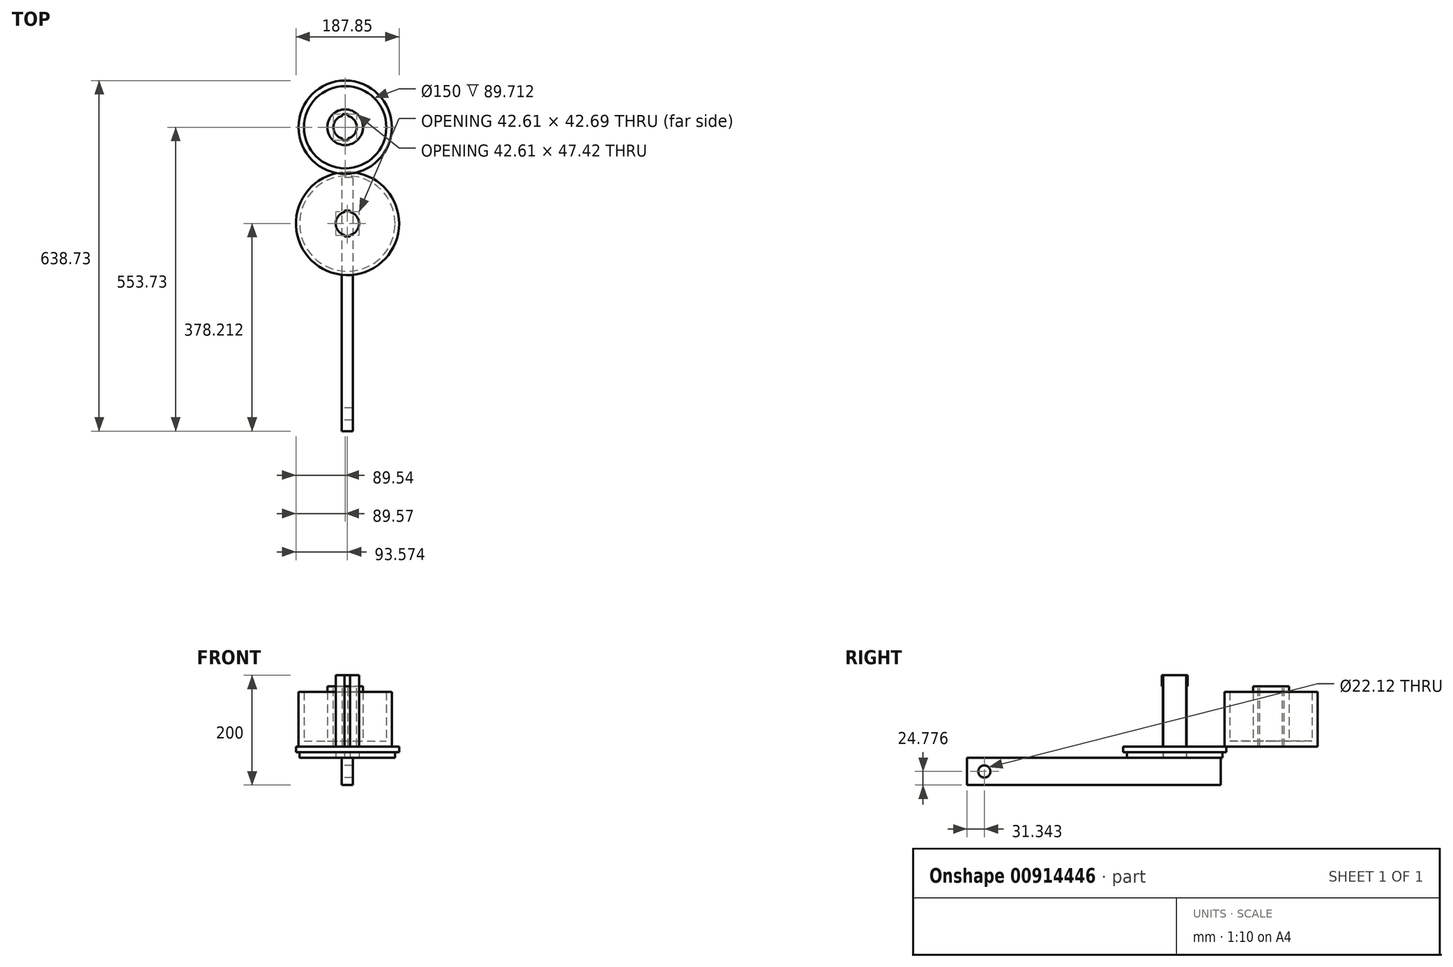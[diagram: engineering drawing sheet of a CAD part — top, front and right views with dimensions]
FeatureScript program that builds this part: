
annotation { "Feature Type Name" : "Feature", "Feature Type Description" : "" }
export const myFeature = defineFeature(function(context is Context, id is Id, definition is map)
    precondition{}
    {
        {
            var Q0;
            Q0=qCreatedBy(makeId("Front.planeOp"),FACE);
            var sketch = newSketch(context, id + "F0", { "sketchPlane" : qUnion([Q0])});
            skLineSegment(sketch, "E0", {"start": v(-85, 100) * mm, "end": v(-85, 0) * mm});
            skLineSegment(sketch, "E1", {"start": v(-85, 0) * mm, "end": v(0, 0) * mm});
            skLineSegment(sketch, "E2", {"start": v(0, 0) * mm, "end": v(0, 10) * mm});
            skLineSegment(sketch, "E3", {"start": v(0, 10) * mm, "end": v(-75, 10) * mm});
            skLineSegment(sketch, "E4", {"start": v(-75, 10) * mm, "end": v(-75, 99.71) * mm});
            skLineSegment(sketch, "E5", {"start": v(-75, 99.71) * mm, "end": v(-85, 100) * mm});
            skSolve(sketch);
        }
        {
            var Q0;
            Q0=makeQuery(id+"F0.imprint","IMPRINT",FACE,{"disambiguationData":[TD([[makeQuery(id+"F0.imprint","IMPRINT",EDGE,{"derivedFrom":sQuery(id+"F0.wireOp",EDGE,"E0")}),1.0]])]});
            var Q1;
            Q1=sQuery(id+"F0.wireOp",EDGE,"E2");
            revolve(context, id + "F1", {"surfaceOperationType" : NewSurfaceOperationType.NEW, "entities" : qUnion([Q0]), "axis" : qUnion([Q1]), "revolveType" : RevolveType.ONE_DIRECTION, "angle" : 360 * degree});
        }
        {
            var Q0;
            Q0=qCreatedBy(makeId("Top.planeOp"),FACE);
            cPlane(context, id + "F2", {"entities" : qUnion([Q0]), "cplaneType" : CPlaneType.OFFSET, "offset" : 110 * mm, "width" : 150 * mm, "height" : 150 * mm});
        }
        {
            var Q0;
            Q0=qCreatedBy(makeId("Top.planeOp"),FACE);
            var sketch = newSketch(context, id + "F3", { "sketchPlane" : qUnion([Q0])});
            skCircle(sketch, "E6", {"center": v(0, 0) * mm, "radius": 32.5 * mm});
            skSolve(sketch);
        }
        {
            var Q0;
            Q0 = qSketchRegion(id + "F3", true);
            extrude(context, id + "F4", {"entities" : qUnion([Q0]), "operationType" : NewBodyOperationType.ADD, "depth" : 110 * mm, "offsetDistance" : 25 * mm});
        }
        {
            var Q0;
            Q0=qCreatedBy(id+"F2.planeOp",FACE);
            cPlane(context, id + "F5", {"entities" : qUnion([Q0]), "cplaneType" : CPlaneType.OFFSET, "offset" : 30 * mm, "width" : 150 * mm, "height" : 150 * mm});
        }
        {
            var Q0;
            Q0=qCreatedBy(id+"F5.planeOp",FACE);
            var sketch = newSketch(context, id + "F6", { "sketchPlane" : qUnion([Q0])});
            skLineSegment(sketch, "E7", {"start": v(4.87, 23.7) * mm, "end": v(-5.13, 23.7) * mm});
            skLineSegment(sketch, "E8", {"start": v(-5.13, 23.7) * mm, "end": v(-5.13, 20.7) * mm});
            skLineSegment(sketch, "E9", {"start": v(4.87, 23.7) * mm, "end": v(4.87, 20.7) * mm});
            skArc(sketch, "E10", {"start": v(-5.13, 20.7) * mm, "mid": v(-21.33, 0) * mm, "end": v(-5.13, -20.7) * mm});
            skArc(sketch, "E11", {"start": v(4.87, 20.7) * mm, "mid": v(21.27, 0) * mm, "end": v(4.87, -20.7) * mm});
            skLineSegment(sketch, "E12", {"start": v(-5.13, -20.7) * mm, "end": v(-5.13, -23.7) * mm});
            skLineSegment(sketch, "E13", {"start": v(-5.13, -23.7) * mm, "end": v(4.87, -23.7) * mm});
            skLineSegment(sketch, "E14", {"start": v(4.87, -23.7) * mm, "end": v(4.87, -20.7) * mm});
            skSolve(sketch);
        }
        {
            var Q0;
            Q0=makeQuery(id+"F6.imprint","IMPRINT",FACE,{"disambiguationData":[TD([[makeQuery(id+"F6.imprint","IMPRINT",EDGE,{"derivedFrom":sQuery(id+"F6.wireOp",EDGE,"E7")}),1.0]])]});
            extrude(context, id + "F7", {"entities" : qUnion([Q0]), "operationType" : NewBodyOperationType.REMOVE, "oppositeDirection" : true, "depth" : 150 * mm, "offsetDistance" : 25 * mm});
        }
        {
            var Q0;
            Q0=qCreatedBy(id+"F2.planeOp",FACE);
            var sketch = newSketch(context, id + "F8", { "sketchPlane" : qUnion([Q0])});
            skLineSegment(sketch, "E15", {"start": v(8.9, -151.8) * mm, "end": v(-1.1, -151.8) * mm});
            skLineSegment(sketch, "E16", {"start": v(-1.1, -151.8) * mm, "end": v(-1.1, -154.8) * mm});
            skLineSegment(sketch, "E17", {"start": v(8.9, -151.8) * mm, "end": v(8.9, -154.8) * mm});
            skArc(sketch, "E18", {"start": v(-1.1, -154.8) * mm, "mid": v(-17.3, -175.52) * mm, "end": v(-1.1, -196.23) * mm});
            skArc(sketch, "E19", {"start": v(8.9, -154.8) * mm, "mid": v(25.3, -175.52) * mm, "end": v(8.9, -196.23) * mm});
            skLineSegment(sketch, "E20", {"start": v(-1.1, -196.23) * mm, "end": v(-1.1, -199.23) * mm});
            skLineSegment(sketch, "E21", {"start": v(-1.1, -199.23) * mm, "end": v(8.9, -199.23) * mm});
            skLineSegment(sketch, "E22", {"start": v(8.9, -199.23) * mm, "end": v(8.9, -196.23) * mm});
            skSolve(sketch);
        }
        {
            var Q0;
            Q0=makeQuery(id+"F8.imprint","IMPRINT",FACE,{"disambiguationData":[TD([[makeQuery(id+"F8.imprint","IMPRINT",EDGE,{"derivedFrom":sQuery(id+"F8.wireOp",EDGE,"E15")}),1.0]])]});
            extrude(context, id + "F9", {"entities" : qUnion([Q0]), "depth" : 20 * mm, "offsetDistance" : 25 * mm});
        }
        {
            var Q0;
            Q0=makeQuery(id+"F9.opExtrude","CAP_FACE",FACE,{"disambiguationData":[OSD([sQuery(id+"F8.wireOp",EDGE,"E15"),sQuery(id+"F8.wireOp",EDGE,"E16"),sQuery(id+"F8.wireOp",EDGE,"E17"),sQuery(id+"F8.wireOp",EDGE,"E18"),sQuery(id+"F8.wireOp",EDGE,"E19"),sQuery(id+"F8.wireOp",EDGE,"E20"),sQuery(id+"F8.wireOp",EDGE,"E21"),sQuery(id+"F8.wireOp",EDGE,"E22")])],"isStart":true});
            var sketch = newSketch(context, id + "F10", { "sketchPlane" : qUnion([Q0])});
            skCircle(sketch, "E23", {"center": v(4.03, 175.52) * mm, "radius": 21.35 * mm});
            skSolve(sketch);
        }
        {
            var Q0;
            {var subQ7=makeQuery(id+"F9.opExtrude","CAP_EDGE",EDGE,{"disambiguationData":[OSD([sQuery(id+"F8.wireOp",EDGE,"E18")])],"isStart":true});Q0=makeQuery(id+"F10.imprint","IMPRINT",FACE,{"disambiguationData":[TD([[makeQuery(id+"F10.imprint","IMPRINT",EDGE,{"derivedFrom":subQ7}),-1.0]])]});}
            extrude(context, id + "F11", {"entities" : qUnion([Q0]), "operationType" : NewBodyOperationType.ADD, "depth" : 130 * mm, "offsetDistance" : 25 * mm});
        }
        {
            var Q0;
            Q0=qCreatedBy(makeId("Top.planeOp"),FACE);
            cPlane(context, id + "F12", {"entities" : qUnion([Q0]), "cplaneType" : CPlaneType.OFFSET, "offset" : 20 * mm, "oppositeDirection" : true, "width" : 150 * mm, "height" : 150 * mm});
        }
        {
            var Q0;
            Q0=makeQuery(id+"F11.opExtrude","CAP_FACE",FACE,{"disambiguationData":[OSD([sQuery(id+"F8.wireOp",EDGE,"E16"),sQuery(id+"F8.wireOp",EDGE,"E17"),sQuery(id+"F8.wireOp",EDGE,"E18"),sQuery(id+"F8.wireOp",EDGE,"E19"),sQuery(id+"F8.wireOp",EDGE,"E20"),sQuery(id+"F8.wireOp",EDGE,"E22"),sQuery(id+"F10.wireOp",EDGE,"E23")])],"isStart":false});
            var sketch = newSketch(context, id + "F13", { "sketchPlane" : qUnion([Q0])});
            skCircle(sketch, "E24", {"center": v(4.03, 175.52) * mm, "radius": 86.95 * mm});
            skSolve(sketch);
        }
        {
            var Q0;
            Q0=makeQuery(id+"F13.imprint","IMPRINT",FACE,{"disambiguationData":[TD([[makeQuery(id+"F13.imprint","IMPRINT",EDGE,{"derivedFrom":sQuery(id+"F13.wireOp",EDGE,"E24")}),1.0]])]});
            extrude(context, id + "F14", {"entities" : qUnion([Q0]), "oppositeDirection" : true, "depth" : 10 * mm, "offsetDistance" : 25 * mm});
        }
        {
            var Q0;
            Q0=qCreatedBy(id+"F12.planeOp",FACE);
            cPlane(context, id + "F15", {"entities" : qUnion([Q0]), "cplaneType" : CPlaneType.OFFSET, "offset" : 20 * mm, "width" : 150 * mm, "height" : 150 * mm});
        }
        {
            var Q0;
            Q0=qCreatedBy(id+"F15.planeOp",FACE);
            var sketch = newSketch(context, id + "F16", { "sketchPlane" : qUnion([Q0])});
            skCircle(sketch, "E25", {"center": v(4.36, -175.55) * mm, "radius": 93.93 * mm});
            skSolve(sketch);
        }
        {
            var Q0;
            Q0=makeQuery(id+"F16.imprint","IMPRINT",FACE,{"disambiguationData":[TD([[makeQuery(id+"F16.imprint","IMPRINT",EDGE,{"derivedFrom":sQuery(id+"F16.wireOp",EDGE,"E25")}),1.0]])]});
            extrude(context, id + "F17", {"entities" : qUnion([Q0]), "oppositeDirection" : true, "depth" : 10 * mm, "offsetDistance" : 25 * mm});
        }
        {
            var Q0;
            Q0=qCreatedBy(id+"F12.planeOp",FACE);
            var sketch = newSketch(context, id + "F18", { "sketchPlane" : qUnion([Q0])});
            skLineSegment(sketch, "E26.bottom", {"start": v(14.05, -91.6) * mm, "end": v(-6.35, -91.6) * mm});
            skLineSegment(sketch, "E26.top", {"start": v(14.05, -553.73) * mm, "end": v(-6.35, -553.73) * mm});
            skLineSegment(sketch, "E26.left", {"start": v(14.05, -91.6) * mm, "end": v(14.05, -553.73) * mm});
            skLineSegment(sketch, "E26.right", {"start": v(-6.35, -91.6) * mm, "end": v(-6.35, -553.73) * mm});
            skSolve(sketch);
        }
        {
            var Q0;
            Q0 = qSketchRegion(id + "F18", true);
            extrude(context, id + "F19", {"entities" : qUnion([Q0]), "oppositeDirection" : true, "depth" : 50 * mm, "offsetDistance" : 25 * mm});
        }
        {
            var Q0;
            Q0=qCreatedBy(makeId("Right.planeOp"),FACE);
            var sketch = newSketch(context, id + "F20", { "sketchPlane" : qUnion([Q0])});
            skCircle(sketch, "E27", {"center": v(-522.39, -45.22) * mm, "radius": 11.06 * mm});
            skSolve(sketch);
        }
        {
            var Q0;
            Q0 = qSketchRegion(id + "F20", true);
            extrude(context, id + "F21", {"entities" : qUnion([Q0]), "operationType" : NewBodyOperationType.REMOVE, "depth" : 50 * mm, "offsetDistance" : 25 * mm});
        }
        {
            var Q0;
            Q0 = qSketchRegion(id + "F20", true);
            extrude(context, id + "F22", {"entities" : qUnion([Q0]), "operationType" : NewBodyOperationType.REMOVE, "oppositeDirection" : true, "depth" : 25 * mm, "offsetDistance" : 25 * mm});
        }
    });
